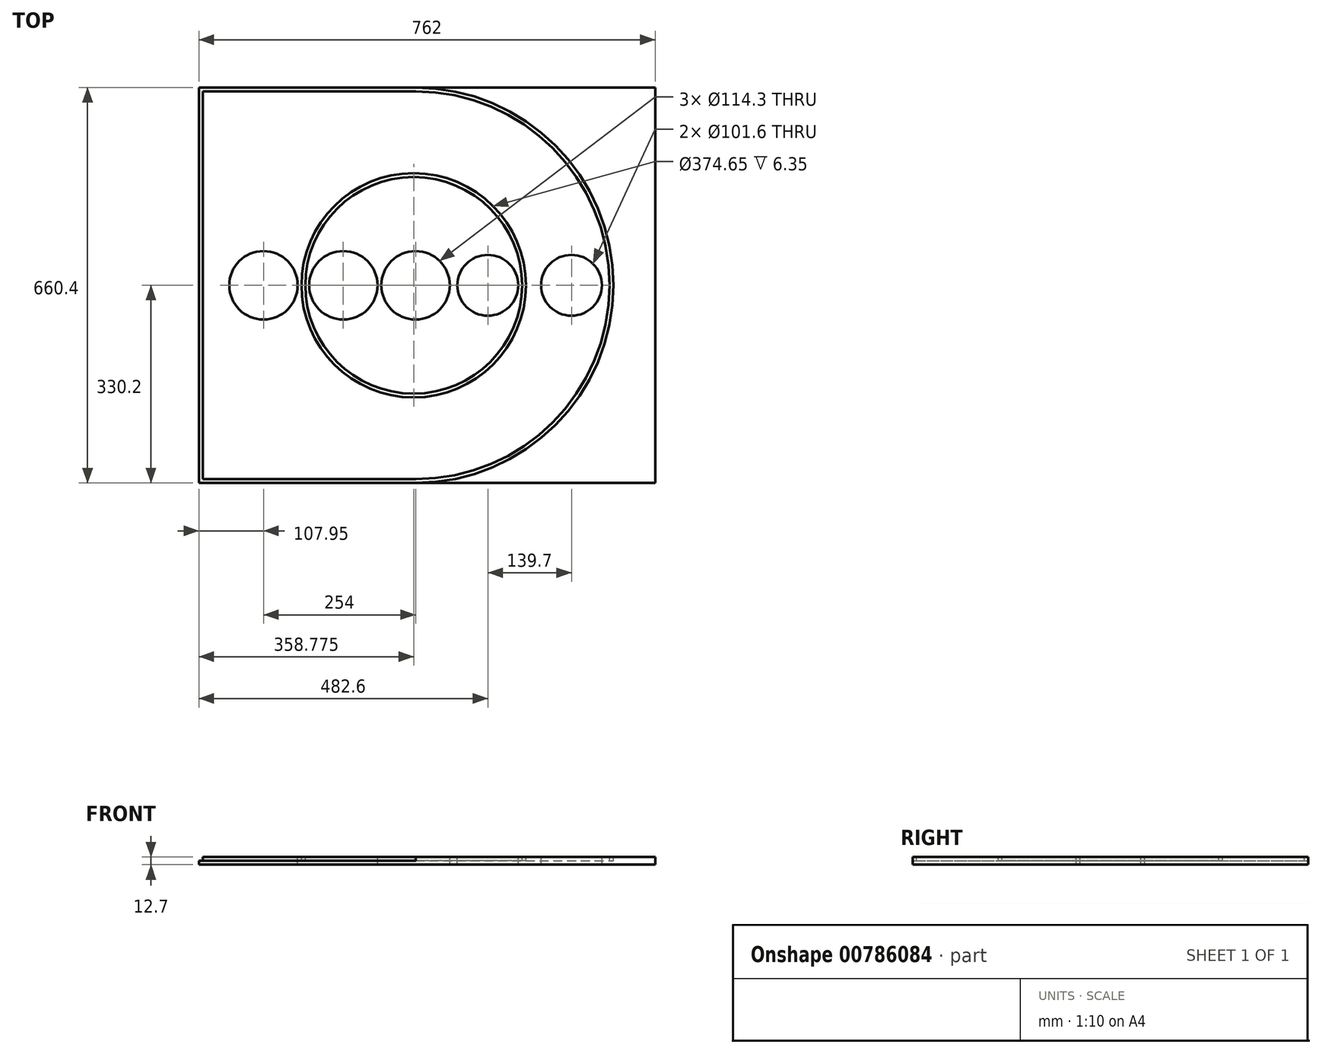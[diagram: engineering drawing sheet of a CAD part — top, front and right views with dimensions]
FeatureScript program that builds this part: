
annotation { "Feature Type Name" : "Feature", "Feature Type Description" : "" }
export const myFeature = defineFeature(function(context is Context, id is Id, definition is map)
    precondition{}
    {
        {
            var Q0;
            Q0=qCreatedBy(makeId("Top.planeOp"),FACE);
            var sketch = newSketch(context, id + "F0", { "sketchPlane" : qUnion([Q0])});
            skLineSegment(sketch, "E0.bottom", {"start": v(0, 0) * mm, "end": v(-762, 0) * mm});
            skLineSegment(sketch, "E0.top", {"start": v(0, 660.4) * mm, "end": v(-762, 660.4) * mm});
            skLineSegment(sketch, "E0.left", {"start": v(0, 0) * mm, "end": v(0, 660.4) * mm});
            skLineSegment(sketch, "E0.right", {"start": v(-762, 0) * mm, "end": v(-762, 660.4) * mm});
            skSolve(sketch);
        }
        {
            var Q0;
            Q0 = qSketchRegion(id + "F0", true);
            extrude(context, id + "F1", {"entities" : qUnion([Q0]), "depth" : 12.7 * mm, "offsetDistance" : 25.4 * mm});
        }
        {
            var Q0;
            Q0=makeQuery(id+"F1.opExtrude","CAP_FACE",FACE,{"disambiguationData":[OSD([sQuery(id+"F0.wireOp",EDGE,"E0.bottom"),sQuery(id+"F0.wireOp",EDGE,"E0.top"),sQuery(id+"F0.wireOp",EDGE,"E0.left"),sQuery(id+"F0.wireOp",EDGE,"E0.right")])],"isStart":false});
            var sketch = newSketch(context, id + "F2", { "sketchPlane" : qUnion([Q0])});
            skLineSegment(sketch, "E1", {"start": v(-762, 330.2) * mm, "end": v(0, 330.2) * mm, "construction": true});
            skCircle(sketch, "E2", {"center": v(-139.7, 330.2) * mm, "radius": 50.8 * mm});
            skCircle(sketch, "E3", {"center": v(-279.4, 330.2) * mm, "radius": 50.8 * mm});
            skCircle(sketch, "E4", {"center": v(-400.05, 330.2) * mm, "radius": 57.15 * mm});
            skCircle(sketch, "E5", {"center": v(-520.7, 330.2) * mm, "radius": 57.15 * mm});
            skCircle(sketch, "E6", {"center": v(-654.05, 330.2) * mm, "radius": 57.15 * mm});
            skSolve(sketch);
        }
        {
            var Q0;
            Q0 = qSketchRegion(id + "F2", true);
            extrude(context, id + "F3", {"entities" : qUnion([Q0]), "operationType" : NewBodyOperationType.REMOVE, "endBound" : BoundingType.THROUGH_ALL, "oppositeDirection" : true, "depth" : 25.4 * mm, "offsetDistance" : 25.4 * mm});
        }
        {
            var Q0;
            Q0=makeQuery(id+"F1.opExtrude","CAP_FACE",FACE,{"disambiguationData":[OSD([sQuery(id+"F0.wireOp",EDGE,"E0.bottom"),sQuery(id+"F0.wireOp",EDGE,"E0.top"),sQuery(id+"F0.wireOp",EDGE,"E0.left"),sQuery(id+"F0.wireOp",EDGE,"E0.right")])],"isStart":false});
            var sketch = newSketch(context, id + "F4", { "sketchPlane" : qUnion([Q0])});
            skArc(sketch, "E7", {"start": v(-400.05, 0) * mm, "mid": v(-69.85, 330.2) * mm, "end": v(-400.05, 660.4) * mm});
            skArc(sketch, "E8.0", {"start": v(-400.05, 6.35) * mm, "mid": v(-76.2, 330.2) * mm, "end": v(-400.05, 654.05) * mm});
            skPoint(sketch, "E9", {"position": v(-76.2, 330.2) * mm});
            skCircle(sketch, "E10.0", {"center": v(-139.7, 330.2) * mm, "radius": 50.8 * mm, "construction": true});
            skLineSegment(sketch, "E11", {"start": v(-400.05, 0) * mm, "end": v(-762, 0) * mm});
            skLineSegment(sketch, "E12", {"start": v(-762, 0) * mm, "end": v(-762, 660.4) * mm});
            skLineSegment(sketch, "E13", {"start": v(-762, 660.4) * mm, "end": v(-400.05, 660.4) * mm});
            skLineSegment(sketch, "E14.1", {"start": v(-755.65, 6.35) * mm, "end": v(-755.65, 654.05) * mm});
            skLineSegment(sketch, "E15", {"start": v(-762, 330.2) * mm, "end": v(0, 330.2) * mm, "construction": true});
            skCircle(sketch, "E16", {"center": v(-403.23, 330.2) * mm, "radius": 180.98 * mm});
            skPoint(sketch, "E17", {"position": v(-222.25, 330.2) * mm});
            skCircle(sketch, "E18.0", {"center": v(-279.4, 330.2) * mm, "radius": 50.8 * mm, "construction": true});
            skCircle(sketch, "E19.0", {"center": v(-403.23, 330.2) * mm, "radius": 187.33 * mm});
            skLineSegment(sketch, "E20", {"start": v(-755.65, 6.35) * mm, "end": v(-400.05, 6.35) * mm});
            skLineSegment(sketch, "E21", {"start": v(-755.65, 654.05) * mm, "end": v(-400.05, 654.05) * mm});
            skSolve(sketch);
        }
        {
            var Q0;
            Q0 = qSketchRegion(id + "F4", true);
            var Q1;
            Q1=makeQuery(id+"F4.imprint","IMPRINT",FACE,{"disambiguationData":[TD([[makeQuery(id+"F4.imprint","IMPRINT",EDGE,{"derivedFrom":sQuery(id+"F4.wireOp",EDGE,"E16")}),-1.0]])]});
            extrude(context, id + "F5", {"entities" : qUnion([Q0, Q1]), "operationType" : NewBodyOperationType.REMOVE, "oppositeDirection" : true, "depth" : 6.35 * mm, "offsetDistance" : 25.4 * mm});
        }
    });
